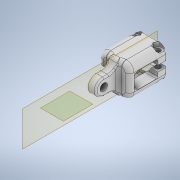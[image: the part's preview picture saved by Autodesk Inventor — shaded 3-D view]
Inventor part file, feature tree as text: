
AUTODESK INVENTOR PART (.ipt)
format: ipt  version: 2022.1 (Build 261234000, 234)  size: 1,031,168 bytes
history: native  units: in
note: dims shown in document units (in); Inventor stores cm internally (conversion verified against a paired STEP export)
features: sketch x26, extrude x24, fillet x20, other x7, projected_geometry x7, hole x2, chamfer x2, mirror x1
ambient origin geometry x8: Origin, YZ Plane, XZ Plane, XY Plane, X Axis, Y Axis, Z Axis, Center Point
bodies: Body1 (feature_tree), Body2 (feature_tree), Body3 (feature_tree), Body4 (feature_tree)
feature tree (89):
  other  "ソリッド1"
  extrude  "押し出し1"  Depth=0.4331in
  extrude  "押し出し2"  Depth=0.5512in
  extrude  "押し出し3"  Depth=0.3937in TaperAngle=0.0deg
  other  "作業平面1"
  extrude  "押し出し4"  Depth=0.315in
  extrude  "押し出し6"  Depth=0.1969in TaperAngle=0.0deg
  extrude  "押し出し5"  Depth=0.1181in
  extrude  "押し出し7"  Depth=0.1181in TaperAngle=0.0deg
  extrude  "押し出し8"  Depth=0.1969in
  fillet  "フィレット1"  Radius=0.1378in
  fillet  "フィレット2"  Radius=0.1969in
  extrude  "押し出し9"  Depth=0.6693in TaperAngle=0.0deg
  extrude  "押し出し10"  Depth=0.1063in
  mirror  "ミラー1"
  extrude  "押し出し11"  Depth=0.1063in
  hole  "穴1"  [1 undecoded]
  sketch  "スケッチ13"
  fillet  "フィレット3"  Radius=0.1181in
  extrude  "押し出し12"  Depth=0.6693in TaperAngle=0.0deg
  extrude  "押し出し13"  Depth=0.815in
  chamfer  "面取り1"  Distance=0.563in
  fillet  "フィレット4"  Radius=0.1417in
  extrude  "押し出し14"  Depth=0.1417in
  fillet  "フィレット5"  Radius=0.4173in
  fillet  "フィレット6"  Radius=0.6693in
  chamfer  "面取り2"  Distance=0.2835in
  extrude  "押し出し15"  Depth=0.4331in TaperAngle=0.0deg
  fillet  "フィレット7"  Radius=0.1378in
  fillet  "フィレット8"  Radius=0.4331in
  extrude  "押し出し16"  Depth=0.3937in
  extrude  "押し出し17"  Depth=0.1181in TaperAngle=0.0deg
  extrude  "押し出し18"  Depth=0.1575in
  hole  "穴3"  [1 undecoded]
  extrude  "押し出し19"  Depth=0.0079in
  extrude  "押し出し20"  Depth=0.0079in
  fillet  "フィレット9"  Radius=0.1575in
  fillet  "フィレット10"  Radius=0.126in
  fillet  "フィレット11"  Radius=0.0787in
  other  "作業平面2"
  extrude  "押し出し21"  TaperAngle=0.0deg  [1 undecoded]
  extrude  "押し出し22"  Depth=0.2205in
  other  "作業平面3"
  extrude  "押し出し23"  Depth=0.2205in
  fillet  "フィレット12"  Radius=0.1969in
  fillet  "フィレット13"  Radius=0.1181in
  fillet  "フィレット14"  Radius=0.2165in
  fillet  "フィレット15"  Radius=0.2165in
  extrude  "押し出し24"  Depth=0.1181in TaperAngle=0.0deg
  fillet  "フィレット16"  Radius=0.0787in
  fillet  "フィレット17"  Radius=0.0118in
  fillet  "フィレット18"  Radius=0.315in
  fillet  "フィレット19"  Radius=0.1969in
  fillet  "フィレット20"  Radius=0.0394in
  sketch  "スケッチ1"
  sketch  "スケッチ2"
  sketch  "スケッチ3"
  sketch  "スケッチ4"
  other  "ソリッド2"
  sketch  "スケッチ5"
  sketch  "スケッチ6"
  other  "ソリッド3"
  sketch  "スケッチ7"
  sketch  "スケッチ8"
  sketch  "スケッチ9"
  other  "ソリッド5"
  sketch  "スケッチ10"
  sketch  "スケッチ11"
  sketch  "スケッチ12"
  sketch  "スケッチ14"
  sketch  "スケッチ15"
  sketch  "スケッチ16"
  sketch  "スケッチ18"
  projected_geometry  "投影ループ1"
  projected_geometry  "投影ループ2"
  sketch  "スケッチ19"
  projected_geometry  "投影ループ3"
  projected_geometry  "投影ループ4"
  projected_geometry  "投影ループ5"
  sketch  "スケッチ20"
  sketch  "スケッチ21"
  sketch  "スケッチ22"
  sketch  "スケッチ23"
  sketch  "スケッチ24"
  sketch  "スケッチ25"
  projected_geometry  "投影ループ6"
  projected_geometry  "投影ループ7"
  sketch  "スケッチ26"
  sketch  "スケッチ27"
note: 3 required parameter values undecoded (feature->parameter linkage not recoverable at this tier; creation-order binding heuristic only, values carry confidence <= 0.55)
